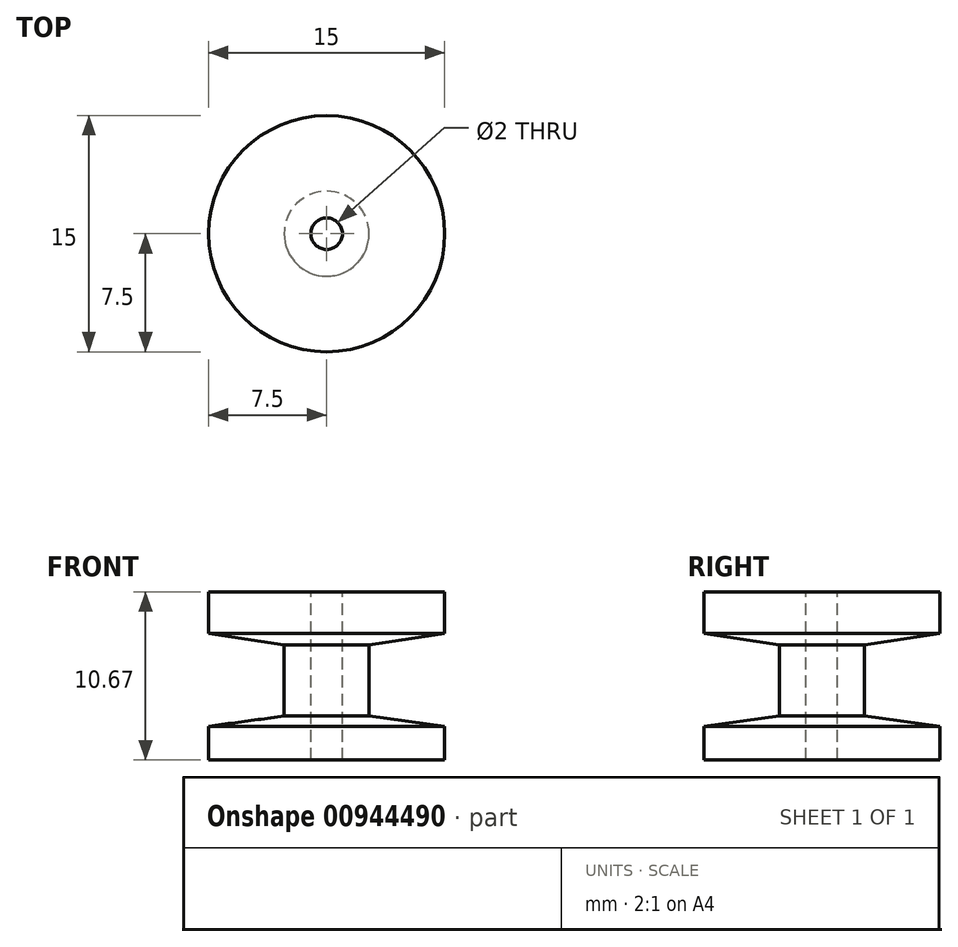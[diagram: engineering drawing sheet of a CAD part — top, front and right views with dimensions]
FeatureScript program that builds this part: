
annotation { "Feature Type Name" : "Feature", "Feature Type Description" : "" }
export const myFeature = defineFeature(function(context is Context, id is Id, definition is map)
    precondition{}
    {
        {
            var Q0;
            Q0=qCreatedBy(makeId("Top.planeOp"),FACE);
            var sketch = newSketch(context, id + "F0", { "sketchPlane" : qUnion([Q0])});
            skCircle(sketch, "E0", {"center": v(0, 0) * mm, "radius": 7.5 * mm});
            skSolve(sketch);
        }
        {
            var Q0;
            Q0=makeQuery(id+"F0.imprint","IMPRINT",FACE,{"disambiguationData":[TD([[makeQuery(id+"F0.imprint","IMPRINT",EDGE,{"derivedFrom":sQuery(id+"F0.wireOp",EDGE,"E0")}),1.0]])]});
            extrude(context, id + "F1", {"entities" : qUnion([Q0]), "depth" : 10.67 * mm, "offsetDistance" : 25.4 * mm});
        }
        {
            var Q0;
            Q0=qCreatedBy(makeId("Right.planeOp"),FACE);
            var sketch = newSketch(context, id + "F2", { "sketchPlane" : qUnion([Q0])});
            skArc(sketch, "E1", {"start": v(-11.61, 7.5) * mm, "mid": v(-13.32, 5.12) * mm, "end": v(-11.59, 2.75) * mm});
            skLineSegment(sketch, "E2", {"start": v(-11.61, 7.5) * mm, "end": v(-11.61, 8.68) * mm});
            skLineSegment(sketch, "E3", {"start": v(-11.59, 2.75) * mm, "end": v(-11.59, 1.58) * mm});
            skLineSegment(sketch, "E4", {"start": v(-2.7, 7.3) * mm, "end": v(-2.7, 2.78) * mm});
            skPoint(sketch, "E5.end.orphan", {"position": v(-2.7, 5.13) * mm});
            skLineSegment(sketch, "E6", {"start": v(-11.61, 8.68) * mm, "end": v(-2.7, 7.3) * mm});
            skLineSegment(sketch, "E7", {"start": v(-11.59, 1.58) * mm, "end": v(-2.7, 2.78) * mm});
            skPoint(sketch, "E8.end.orphan", {"position": v(-2.7, 8.68) * mm});
            skPoint(sketch, "E9.orphan", {"position": v(-2.7, 1.58) * mm});
            skSolve(sketch);
        }
        {
            var Q0;
            Q0=makeQuery(id+"F2.imprint","IMPRINT",FACE,{"disambiguationData":[TD([[makeQuery(id+"F2.imprint","IMPRINT",EDGE,{"derivedFrom":sQuery(id+"F2.wireOp",EDGE,"E1")}),1.0]])]});
            var Q1;
            Q1=makeQuery(id+"F1.opExtrude","SWEPT_FACE",FACE,{"disambiguationData":[OSD([sQuery(id+"F0.wireOp",EDGE,"E0")])]});
            revolve(context, id + "F3", {"operationType" : NewBodyOperationType.REMOVE, "surfaceOperationType" : NewSurfaceOperationType.NEW, "entities" : qUnion([Q0]), "axis" : qUnion([Q1]), "revolveType" : RevolveType.FULL, "oppositeDirection" : true});
        }
        {
            var Q0;
            Q0=makeQuery(id+"F1.opExtrude","CAP_FACE",FACE,{"disambiguationData":[OSD([sQuery(id+"F0.wireOp",EDGE,"E0")])],"isStart":false});
            var sketch = newSketch(context, id + "F4", { "sketchPlane" : qUnion([Q0])});
            skCircle(sketch, "E10", {"center": v(0, 0) * mm, "radius": 0.75 * mm});
            skSolve(sketch);
        }
        {
            var Q0;
            Q0=sQuery(id+"F4.wireOp",VERTEX,"E10.center");
            var Q1;
            Q1=makeQuery(id+"F1.opExtrude","SWEPT_BODY",BODY,{"disambiguationData":[OSD([sQuery(id+"F0.wireOp",EDGE,"E0")])]});
            hole(context, id + "F5", {"style" : HoleStyle.SIMPLE, "endStyle" : HoleEndStyle.THROUGH, "holeDiameter" : 2 * mm, "majorDiameter" : 5 * mm, "isTappedThrough" : true, "tappedDepth" : 12 * mm, "tapClearance" : 3, "locations" : qUnion([Q0]), "scope" : qUnion([Q1])});
        }
    });
